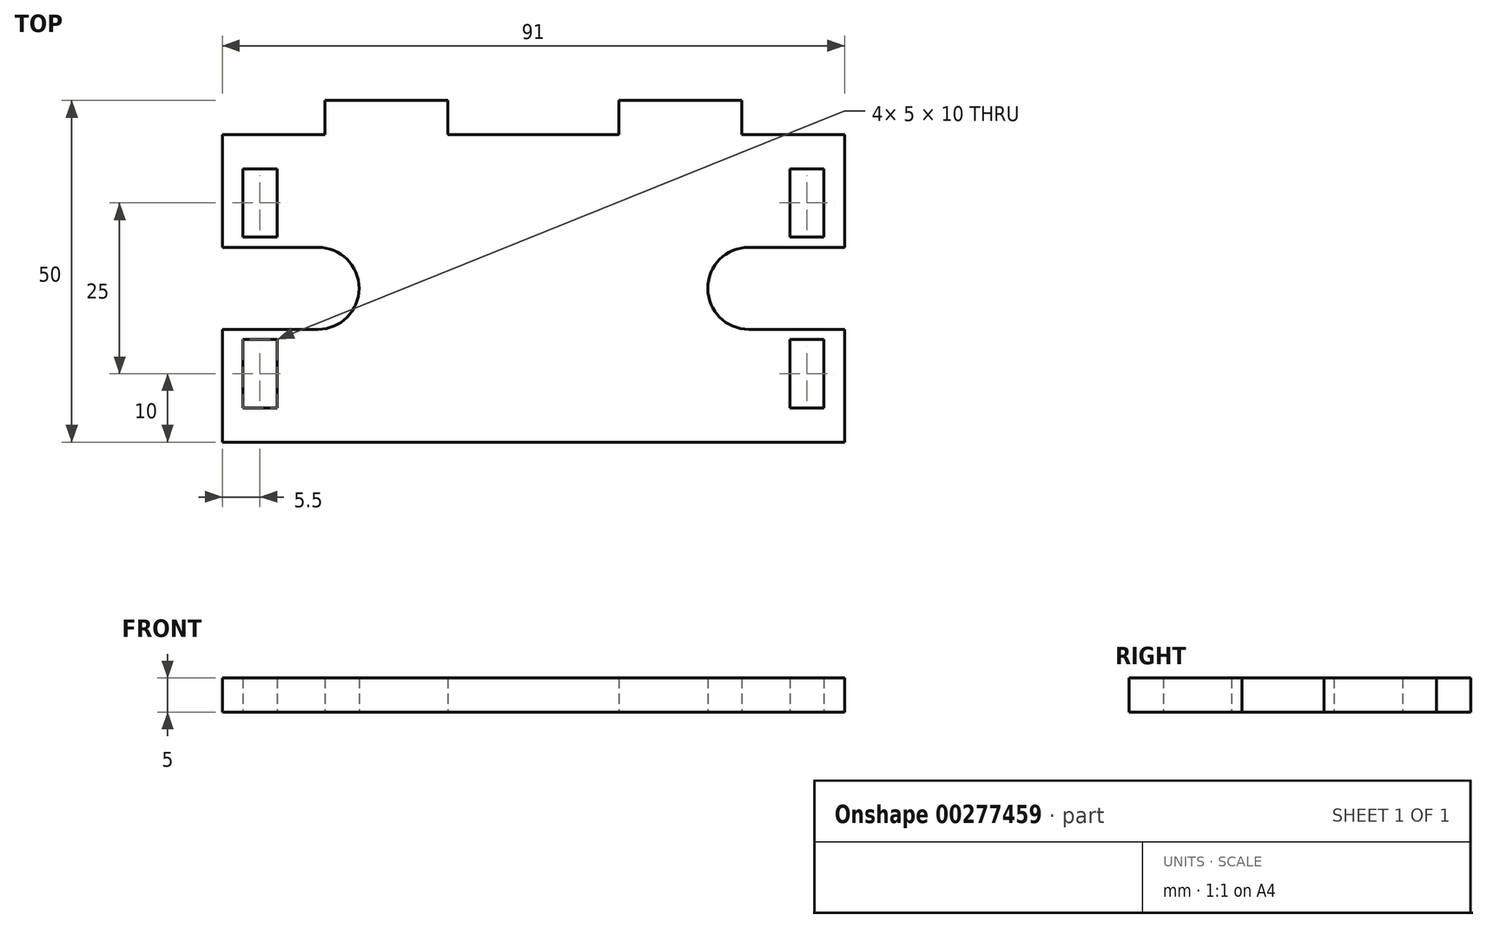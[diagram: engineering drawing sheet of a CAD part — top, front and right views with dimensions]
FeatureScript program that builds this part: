
annotation { "Feature Type Name" : "Feature", "Feature Type Description" : "" }
export const myFeature = defineFeature(function(context is Context, id is Id, definition is map)
    precondition{}
    {
        {
            var Q0;
            Q0=qCreatedBy(makeId("Top.planeOp"),FACE);
            var sketch = newSketch(context, id + "F0", { "sketchPlane" : qUnion([Q0])});
            skLineSegment(sketch, "E0.bottom", {"start": v(-45.5, 22.5) * mm, "end": v(-30.5, 22.5) * mm});
            skLineSegment(sketch, "E0.top", {"start": v(-45.5, -22.5) * mm, "end": v(45.5, -22.5) * mm});
            skLineSegment(sketch, "E0.left", {"start": v(-45.5, 22.5) * mm, "end": v(-45.5, 6) * mm});
            skLineSegment(sketch, "E0.right", {"start": v(45.5, 22.5) * mm, "end": v(45.5, 6) * mm});
            skLineSegment(sketch, "E1.top", {"start": v(-30.5, 27.5) * mm, "end": v(-12.5, 27.5) * mm});
            skLineSegment(sketch, "E1.left", {"start": v(-30.5, 22.5) * mm, "end": v(-30.5, 27.5) * mm});
            skLineSegment(sketch, "E1.right", {"start": v(-12.5, 22.5) * mm, "end": v(-12.5, 27.5) * mm});
            skLineSegment(sketch, "E2.top", {"start": v(12.5, 27.5) * mm, "end": v(30.5, 27.5) * mm});
            skLineSegment(sketch, "E2.left", {"start": v(12.5, 22.5) * mm, "end": v(12.5, 27.5) * mm});
            skLineSegment(sketch, "E2.right", {"start": v(30.5, 22.5) * mm, "end": v(30.5, 27.5) * mm});
            skLineSegment(sketch, "E3.bottom", {"start": v(-42.5, 17.5) * mm, "end": v(-37.5, 17.5) * mm});
            skLineSegment(sketch, "E3.top", {"start": v(-42.5, 7.5) * mm, "end": v(-37.5, 7.5) * mm});
            skLineSegment(sketch, "E3.left", {"start": v(-42.5, 17.5) * mm, "end": v(-42.5, 7.5) * mm});
            skLineSegment(sketch, "E3.right", {"start": v(-37.5, 17.5) * mm, "end": v(-37.5, 7.5) * mm});
            skLineSegment(sketch, "E4.bottom", {"start": v(-42.5, -7.5) * mm, "end": v(-37.5, -7.5) * mm});
            skLineSegment(sketch, "E4.top", {"start": v(-42.5, -17.5) * mm, "end": v(-37.5, -17.5) * mm});
            skLineSegment(sketch, "E4.left", {"start": v(-42.5, -7.5) * mm, "end": v(-42.5, -17.5) * mm});
            skLineSegment(sketch, "E4.right", {"start": v(-37.5, -7.5) * mm, "end": v(-37.5, -17.5) * mm});
            skLineSegment(sketch, "E5.bottom", {"start": v(42.5, 17.5) * mm, "end": v(37.5, 17.5) * mm});
            skLineSegment(sketch, "E5.top", {"start": v(42.5, 7.5) * mm, "end": v(37.5, 7.5) * mm});
            skLineSegment(sketch, "E5.left", {"start": v(42.5, 17.5) * mm, "end": v(42.5, 7.5) * mm});
            skLineSegment(sketch, "E5.right", {"start": v(37.5, 17.5) * mm, "end": v(37.5, 7.5) * mm});
            skLineSegment(sketch, "E6.bottom", {"start": v(42.5, -7.5) * mm, "end": v(37.5, -7.5) * mm});
            skLineSegment(sketch, "E6.top", {"start": v(42.5, -17.5) * mm, "end": v(37.5, -17.5) * mm});
            skLineSegment(sketch, "E6.left", {"start": v(42.5, -7.5) * mm, "end": v(42.5, -17.5) * mm});
            skLineSegment(sketch, "E6.right", {"start": v(37.5, -7.5) * mm, "end": v(37.5, -17.5) * mm});
            skLineSegment(sketch, "E7.trimOffspring", {"start": v(-12.5, 22.5) * mm, "end": v(12.5, 22.5) * mm});
            skLineSegment(sketch, "E8.trimOffspring", {"start": v(30.5, 22.5) * mm, "end": v(45.5, 22.5) * mm});
            skArc(sketch, "E9", {"start": v(-31.5, -6) * mm, "mid": v(-25.5, 0) * mm, "end": v(-31.5, 6) * mm});
            skArc(sketch, "E10", {"start": v(31.5, 6) * mm, "mid": v(25.5, 0) * mm, "end": v(31.5, -6) * mm});
            skLineSegment(sketch, "E11", {"start": v(-31.5, 6) * mm, "end": v(-45.5, 6) * mm});
            skLineSegment(sketch, "E12", {"start": v(-31.5, -6) * mm, "end": v(-45.5, -6) * mm});
            skLineSegment(sketch, "E13.trimOffspring", {"start": v(-45.5, -6) * mm, "end": v(-45.5, -22.5) * mm});
            skLineSegment(sketch, "E14", {"start": v(31.5, 6) * mm, "end": v(45.5, 6) * mm});
            skLineSegment(sketch, "E15", {"start": v(31.5, -6) * mm, "end": v(45.5, -6) * mm});
            skLineSegment(sketch, "E16.trimOffspring", {"start": v(45.5, -6) * mm, "end": v(45.5, -22.5) * mm});
            skLineSegment(sketch, "E17", {"start": v(0, 0) * mm, "end": v(0, -22.5) * mm, "construction": true});
            skSolve(sketch);
        }
        {
            var Q0;
            Q0=makeQuery(id+"F0.imprint","IMPRINT",FACE,{"disambiguationData":[TD([[makeQuery(id+"F0.imprint","IMPRINT",EDGE,{"derivedFrom":sQuery(id+"F0.wireOp",EDGE,"E0.bottom")}),-1.0]])]});
            extrude(context, id + "F1", {"entities" : qUnion([Q0]), "depth" : 5 * mm});
        }
    });
